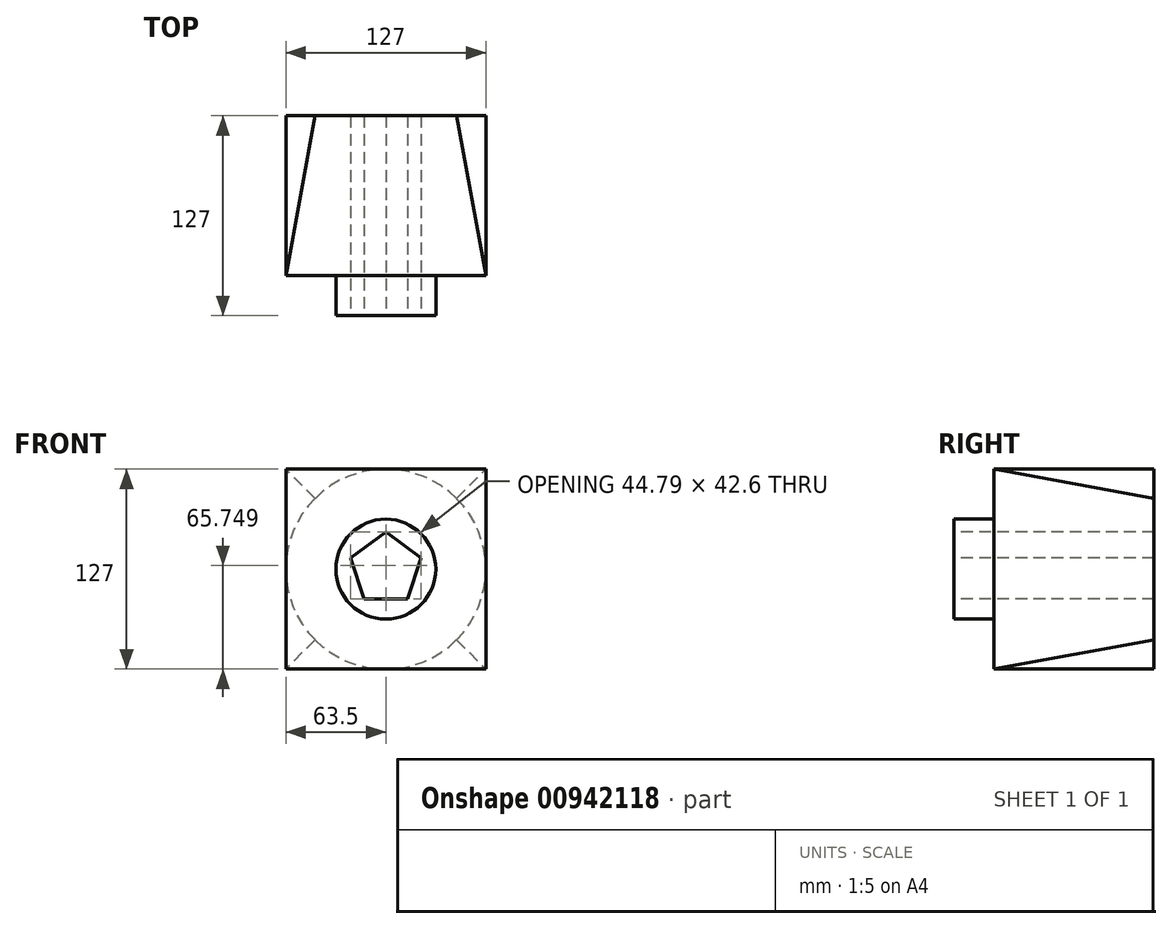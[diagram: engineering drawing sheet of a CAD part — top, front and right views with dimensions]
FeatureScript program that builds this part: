
annotation { "Feature Type Name" : "Feature", "Feature Type Description" : "" }
export const myFeature = defineFeature(function(context is Context, id is Id, definition is map)
    precondition{}
    {
        {
            var Q0;
            Q0=qCreatedBy(makeId("Front.planeOp"),FACE);
            var sketch = newSketch(context, id + "F0", { "sketchPlane" : qUnion([Q0])});
            skCircle(sketch, "E0", {"center": v(0, 0) * mm, "radius": 63.5 * mm});
            skSolve(sketch);
        }
        {
            var Q0;
            Q0=qCreatedBy(makeId("Front.planeOp"),FACE);
            cPlane(context, id + "F1", {"entities" : qUnion([Q0]), "cplaneType" : CPlaneType.OFFSET, "offset" : 101.6 * mm, "width" : 152.4 * mm, "height" : 152.4 * mm});
        }
        {
            var Q0;
            Q0=qCreatedBy(id+"F1.planeOp",FACE);
            var sketch = newSketch(context, id + "F2", { "sketchPlane" : qUnion([Q0])});
            skLineSegment(sketch, "E1.bottom", {"start": v(-63.5, -63.5) * mm, "end": v(63.5, -63.5) * mm});
            skLineSegment(sketch, "E1.top", {"start": v(-63.5, 63.5) * mm, "end": v(63.5, 63.5) * mm});
            skLineSegment(sketch, "E1.left", {"start": v(-63.5, -63.5) * mm, "end": v(-63.5, 63.5) * mm});
            skLineSegment(sketch, "E1.right", {"start": v(63.5, -63.5) * mm, "end": v(63.5, 63.5) * mm});
            skPoint(sketch, "E1.middle", {"position": v(0, 0) * mm});
            skSolve(sketch);
        }
        {
            var Q0;
            Q0 = qSketchRegion(id + "F0", true);
            var Q1;
            Q1 = qSketchRegion(id + "F2", true);
            loft(context, id + "F3", {"sheetProfilesArray" : [{ "sheetProfileEntities" : qUnion([Q0]) }, { "sheetProfileEntities" : qUnion([Q1]) }]});
        }
        {
            var Q0;
            Q0=makeQuery(id+"F3.opLoft","CAP_FACE",FACE,{"disambiguationData":[OSD([makeQuery(id+"F2.imprint","IMPRINT",FACE,{"disambiguationData":[TD([[makeQuery(id+"F2.imprint","IMPRINT",EDGE,{"derivedFrom":sQuery(id+"F2.wireOp",EDGE,"E1.bottom")}),1.0]])]})])],"isStart":true});
            var sketch = newSketch(context, id + "F4", { "sketchPlane" : qUnion([Q0])});
            skCircle(sketch, "E2", {"center": v(0, 0) * mm, "radius": 31.75 * mm});
            skSolve(sketch);
        }
        {
            var Q0;
            Q0 = qSketchRegion(id + "F4", true);
            extrude(context, id + "F5", {"entities" : qUnion([Q0]), "operationType" : NewBodyOperationType.ADD, "depth" : 25.4 * mm, "offsetDistance" : 25.4 * mm});
        }
        {
            var Q0;
            Q0=makeQuery(id+"F5.opExtrude","CAP_FACE",FACE,{"disambiguationData":[OSD([sQuery(id+"F4.wireOp",EDGE,"E2")])],"isStart":false});
            var sketch = newSketch(context, id + "F6", { "sketchPlane" : qUnion([Q0])});
            skCircle(sketch, "E3.cCircle", {"center": v(0, 0) * mm, "radius": 19.05 * mm, "construction": true});
            skLineSegment(sketch, "E3.0", {"start": v(-13.84, -19.05) * mm, "end": v(-22.4, 7.28) * mm});
            skLineSegment(sketch, "E3.1", {"start": v(-22.4, 7.28) * mm, "end": v(0, 23.55) * mm});
            skLineSegment(sketch, "E3.2", {"start": v(0, 23.55) * mm, "end": v(22.4, 7.28) * mm});
            skLineSegment(sketch, "E3.3", {"start": v(22.4, 7.28) * mm, "end": v(13.84, -19.05) * mm});
            skLineSegment(sketch, "E3.4", {"start": v(13.84, -19.05) * mm, "end": v(-13.84, -19.05) * mm});
            skPoint(sketch, "E3.0.midPoint", {"position": v(-18.12, -5.89) * mm});
            skSolve(sketch);
        }
        {
            var Q0;
            Q0 = qSketchRegion(id + "F6", true);
            extrude(context, id + "F7", {"entities" : qUnion([Q0]), "operationType" : NewBodyOperationType.REMOVE, "oppositeDirection" : true, "depth" : 127 * mm, "offsetDistance" : 25.4 * mm});
        }
    });
